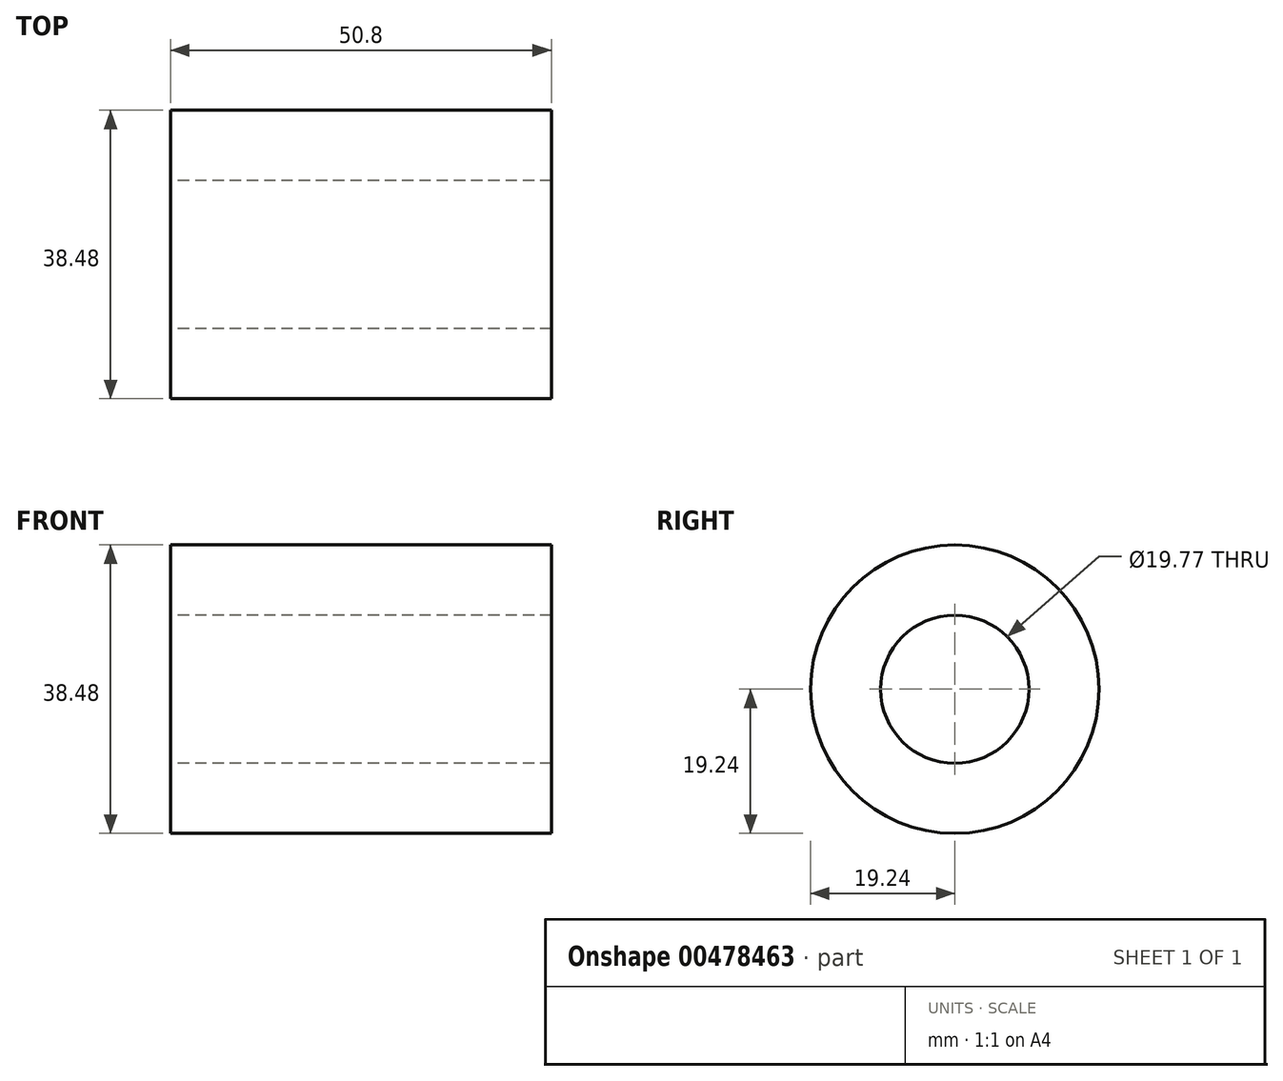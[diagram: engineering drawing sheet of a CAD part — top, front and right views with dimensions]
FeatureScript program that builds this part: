
annotation { "Feature Type Name" : "Feature", "Feature Type Description" : "" }
export const myFeature = defineFeature(function(context is Context, id is Id, definition is map)
    precondition{}
    {
        {
            var Q0;
            Q0=qCreatedBy(makeId("Right.planeOp"),FACE);
            var sketch = newSketch(context, id + "F0", { "sketchPlane" : qUnion([Q0])});
            skCircle(sketch, "E0", {"center": v(0, 0) * mm, "radius": 19.24 * mm});
            skCircle(sketch, "E1", {"center": v(0, 0) * mm, "radius": 9.89 * mm});
            skSolve(sketch);
        }
        {
            var Q0;
            Q0=makeQuery(id+"F0.imprint","IMPRINT",FACE,{"disambiguationData":[TD([[makeQuery(id+"F0.imprint","IMPRINT",EDGE,{"derivedFrom":sQuery(id+"F0.wireOp",EDGE,"E0")}),1.0]])]});
            extrude(context, id + "F1", {"entities" : qUnion([Q0]), "depth" : 50.8 * mm});
        }
    });
